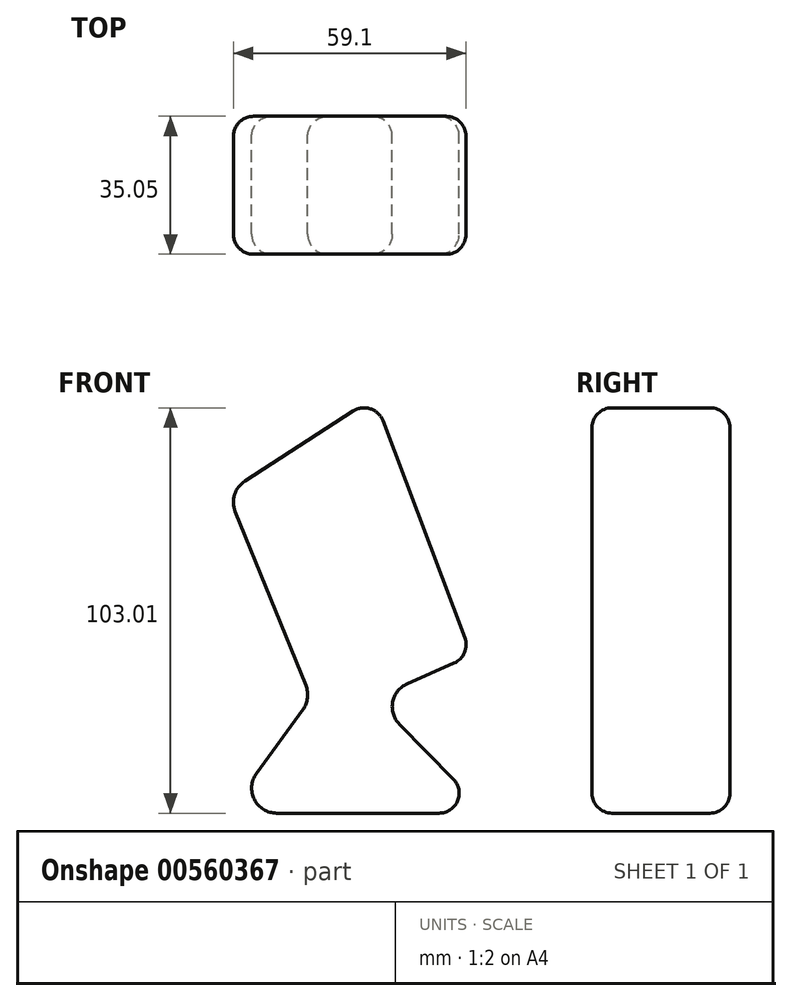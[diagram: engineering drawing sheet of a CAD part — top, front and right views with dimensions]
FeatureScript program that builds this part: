
annotation { "Feature Type Name" : "Feature", "Feature Type Description" : "" }
export const myFeature = defineFeature(function(context is Context, id is Id, definition is map)
    precondition{}
    {
        {
            var Q0;
            Q0=qCreatedBy(makeId("Front.planeOp"),FACE);
            var sketch = newSketch(context, id + "F0", { "sketchPlane" : qUnion([Q0])});
            skLineSegment(sketch, "E0", {"start": v(6.44, -6.55) * mm, "end": v(28.66, -29.16) * mm});
            skLineSegment(sketch, "E1", {"start": v(28.66, -29.16) * mm, "end": v(-24.75, -29.16) * mm});
            skLineSegment(sketch, "E2", {"start": v(-29.88, -19.07) * mm, "end": v(-18.07, -2.85) * mm});
            skLineSegment(sketch, "E3", {"start": v(-17.32, 3.27) * mm, "end": v(-35.25, 47.49) * mm});
            skLineSegment(sketch, "E4", {"start": v(-32.82, 55.2) * mm, "end": v(0, 76.46) * mm});
            skLineSegment(sketch, "E5", {"start": v(0, 76.46) * mm, "end": v(24.76, 10.92) * mm});
            skLineSegment(sketch, "E6", {"start": v(24.76, 10.92) * mm, "end": v(8.4, 3.7) * mm});
            skPoint(sketch, "E7.visualSharp", {"position": v(-37.22, -29.16) * mm});
            skArc(sketch, "E7.filletArc", {"start": v(-30.93, -24.24) * mm, "mid": v(-28.7, -27.78) * mm, "end": v(-24.75, -29.16) * mm});
            skPoint(sketch, "E8.visualSharp", {"position": v(-29.88, -19.07) * mm});
            skArc(sketch, "E8.filletArc", {"start": v(-29.88, -19.07) * mm, "mid": v(-30.97, -21.54) * mm, "end": v(-30.93, -24.24) * mm});
            skPoint(sketch, "E9.visualSharp", {"position": v(0, 0) * mm});
            skArc(sketch, "E9.filletArc", {"start": v(8.4, 3.7) * mm, "mid": v(4.73, -0.9) * mm, "end": v(6.44, -6.55) * mm});
            skPoint(sketch, "E10.visualSharp", {"position": v(-16, 0) * mm});
            skArc(sketch, "E10.filletArc", {"start": v(-18.07, -2.85) * mm, "mid": v(-16.9, 0.11) * mm, "end": v(-17.32, 3.27) * mm});
            skPoint(sketch, "E11.visualSharp", {"position": v(-37.22, 52.35) * mm});
            skArc(sketch, "E11.filletArc", {"start": v(-32.82, 55.2) * mm, "mid": v(-35.42, 51.78) * mm, "end": v(-35.25, 47.49) * mm});
            skSolve(sketch);
        }
        {
            var Q0;
            Q0 = qSketchRegion(id + "F0", true);
            extrude(context, id + "F1", {"entities" : qUnion([Q0]), "depth" : 35.05 * mm, "offsetDistance" : 25.4 * mm});
        }
        {
            var Q0;
            Q0=makeQuery(id+"F1.opExtrude","SWEPT_EDGE",EDGE,{"disambiguationData":[OSD([sQuery(id+"F0.wireOp",EDGE,"E4"),sQuery(id+"F0.wireOp",EDGE,"E5")])]});
            var Q1;
            Q1=makeQuery(id+"F1.opExtrude","SWEPT_EDGE",EDGE,{"disambiguationData":[OSD([sQuery(id+"F0.wireOp",EDGE,"E5"),sQuery(id+"F0.wireOp",EDGE,"E6")])]});
            var Q2;
            Q2=makeQuery(id+"F1.opExtrude","SWEPT_FACE",FACE,{"disambiguationData":[OSD([sQuery(id+"F0.wireOp",EDGE,"E2")])]});
            var Q3;
            Q3=makeQuery(id+"F1.opExtrude","SWEPT_FACE",FACE,{"disambiguationData":[OSD([sQuery(id+"F0.wireOp",EDGE,"E0")])]});
            var Q4;
            Q4=makeQuery(id+"F1.opExtrude","SWEPT_FACE",FACE,{"disambiguationData":[OSD([sQuery(id+"F0.wireOp",EDGE,"E5")])]});
            fillet(context, id + "F2", {"entities" : qUnion([Q0, Q1, Q2, Q3, Q4]), "radius" : 5.08 * mm, "tangentPropagation" : true, "allowEdgeOverflow" : false});
        }
    });
